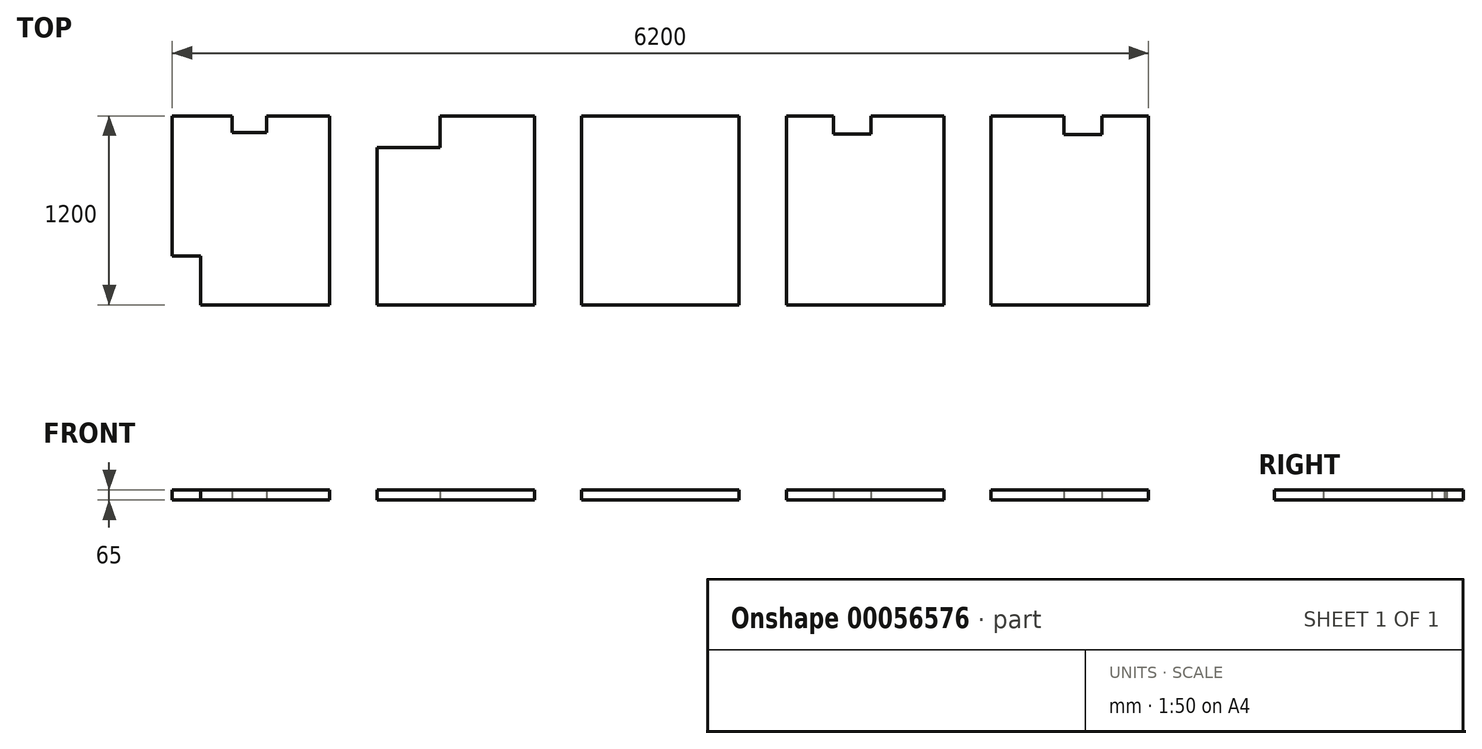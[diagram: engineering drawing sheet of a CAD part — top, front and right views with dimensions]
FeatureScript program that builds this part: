
annotation { "Feature Type Name" : "Feature", "Feature Type Description" : "" }
export const myFeature = defineFeature(function(context is Context, id is Id, definition is map)
    precondition{}
    {
        {
            var Q0;
            Q0=qCreatedBy(makeId("Top.planeOp"),FACE);
            var sketch = newSketch(context, id + "F0", { "sketchPlane" : qUnion([Q0])});
            skLineSegment(sketch, "E0.bottom", {"start": v(-563.41, 568.52) * mm, "end": v(-183.41, 568.52) * mm});
            skLineSegment(sketch, "E0.top", {"start": v(-383.41, -631.48) * mm, "end": v(436.59, -631.48) * mm});
            skLineSegment(sketch, "E0.left", {"start": v(-563.41, 568.52) * mm, "end": v(-563.41, -321.48) * mm});
            skLineSegment(sketch, "E0.right", {"start": v(436.59, 568.52) * mm, "end": v(436.59, -631.48) * mm});
            skLineSegment(sketch, "E1.top", {"start": v(-563.41, -321.48) * mm, "end": v(-383.41, -321.48) * mm});
            skLineSegment(sketch, "E1.right", {"start": v(-383.41, -631.48) * mm, "end": v(-383.41, -321.48) * mm});
            skLineSegment(sketch, "E2.top", {"start": v(-183.41, 463.52) * mm, "end": v(36.59, 463.52) * mm});
            skLineSegment(sketch, "E2.left", {"start": v(-183.41, 568.52) * mm, "end": v(-183.41, 463.52) * mm});
            skLineSegment(sketch, "E2.right", {"start": v(36.59, 568.52) * mm, "end": v(36.59, 463.52) * mm});
            skLineSegment(sketch, "E3.trimOffspring", {"start": v(36.59, 568.52) * mm, "end": v(436.59, 568.52) * mm});
            skLineSegment(sketch, "E4.bottom", {"start": v(1136.59, 568.52) * mm, "end": v(1736.59, 568.52) * mm});
            skLineSegment(sketch, "E4.top", {"start": v(736.59, -631.48) * mm, "end": v(1736.59, -631.48) * mm});
            skLineSegment(sketch, "E4.left", {"start": v(736.59, 368.52) * mm, "end": v(736.59, -631.48) * mm});
            skLineSegment(sketch, "E4.right", {"start": v(1736.59, 568.52) * mm, "end": v(1736.59, -631.48) * mm});
            skLineSegment(sketch, "E5.top", {"start": v(736.59, 368.52) * mm, "end": v(1136.59, 368.52) * mm});
            skLineSegment(sketch, "E5.right", {"start": v(1136.59, 568.52) * mm, "end": v(1136.59, 368.52) * mm});
            skLineSegment(sketch, "E6.bottom", {"start": v(2036.59, 568.52) * mm, "end": v(3036.59, 568.52) * mm});
            skLineSegment(sketch, "E6.top", {"start": v(2036.59, -631.48) * mm, "end": v(3036.59, -631.48) * mm});
            skLineSegment(sketch, "E6.left", {"start": v(2036.59, 568.52) * mm, "end": v(2036.59, -631.48) * mm});
            skLineSegment(sketch, "E6.right", {"start": v(3036.59, 568.52) * mm, "end": v(3036.59, -631.48) * mm});
            skLineSegment(sketch, "E7.bottom", {"start": v(3336.59, 568.52) * mm, "end": v(3635.59, 568.52) * mm});
            skLineSegment(sketch, "E7.top", {"start": v(3336.59, -631.48) * mm, "end": v(4336.59, -631.48) * mm});
            skLineSegment(sketch, "E7.left", {"start": v(3336.59, 568.52) * mm, "end": v(3336.59, -631.48) * mm});
            skLineSegment(sketch, "E7.right", {"start": v(4336.59, 568.52) * mm, "end": v(4336.59, -631.48) * mm});
            skLineSegment(sketch, "E8.top", {"start": v(3635.59, 453.52) * mm, "end": v(3875.59, 453.52) * mm});
            skLineSegment(sketch, "E8.left", {"start": v(3635.59, 568.52) * mm, "end": v(3635.59, 453.52) * mm});
            skLineSegment(sketch, "E8.right", {"start": v(3875.59, 568.52) * mm, "end": v(3875.59, 453.52) * mm});
            skLineSegment(sketch, "E9.trimOffspring", {"start": v(3875.59, 568.52) * mm, "end": v(4336.59, 568.52) * mm});
            skLineSegment(sketch, "E10.bottom", {"start": v(4636.59, 568.52) * mm, "end": v(5100.59, 568.52) * mm});
            skLineSegment(sketch, "E10.top", {"start": v(4636.59, -631.48) * mm, "end": v(5636.59, -631.48) * mm});
            skLineSegment(sketch, "E10.left", {"start": v(4636.59, 568.52) * mm, "end": v(4636.59, -631.48) * mm});
            skLineSegment(sketch, "E10.right", {"start": v(5636.59, 568.52) * mm, "end": v(5636.59, -631.48) * mm});
            skLineSegment(sketch, "E11.top", {"start": v(5100.59, 448.52) * mm, "end": v(5340.59, 448.52) * mm});
            skLineSegment(sketch, "E11.left", {"start": v(5100.59, 568.52) * mm, "end": v(5100.59, 448.52) * mm});
            skLineSegment(sketch, "E11.right", {"start": v(5340.59, 568.52) * mm, "end": v(5340.59, 448.52) * mm});
            skLineSegment(sketch, "E12.trimOffspring", {"start": v(5340.59, 568.52) * mm, "end": v(5636.59, 568.52) * mm});
            skSolve(sketch);
        }
        {
            var Q0;
            Q0 = qSketchRegion(id + "F0", true);
            extrude(context, id + "F1", {"entities" : qUnion([Q0]), "depth" : 65 * mm});
        }
    });
